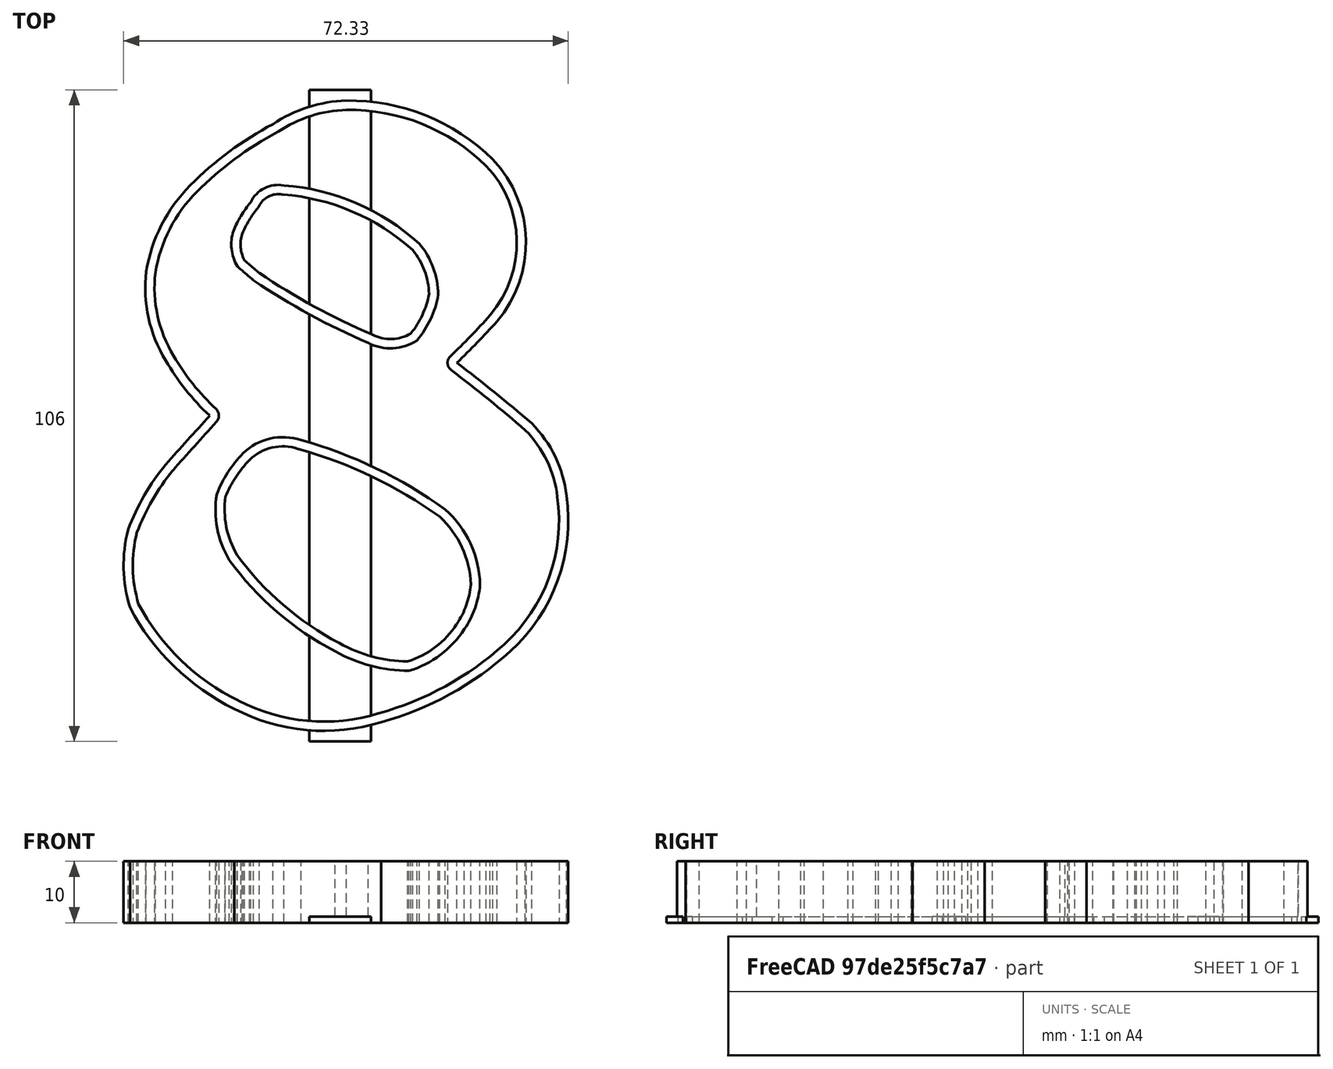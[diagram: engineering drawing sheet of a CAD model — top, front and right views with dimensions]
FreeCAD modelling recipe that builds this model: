
FCSTD DOCUMENT  (FreeCAD 0.20R27319 (Git))
Label: NumberCutter_8
License: All rights reserved
LicenseURL: http://en.wikipedia.org/wiki/All_rights_reserved
objects: Image::ImagePlane×1, Sketcher::SketchObject×1, PartDesign::Body×1, Part::Offset2D×1, Part::Extrusion×1, Part::Box×1, Part::MultiFuse×1
note: 6 computed .brp shape members not serialized (recipe doc carries the construction recipe); baked Part::Feature solids carry a one-line shape summary decoded from their .brp

FEATURE [Image::ImagePlane] ImagePlane
  XSize = 70
  YSize = 100
FEATURE [Sketcher::SketchObject] Sketch
  FullyConstrained = false
  MapMode = 5
  Support = -> [XY_Plane]
  sketch-geometry (35):
    g0: ArcOfCircle CenterX=0.458815 CenterY=17.8982 CenterZ=0 NormalX=0 NormalY=0 NormalZ=1 AngleXU=0 Radius=33.3475 StartAngle=0.793382 EndAngle=1.58456
    g1: ArcOfCircle CenterX=9.51677 CenterY=28.1376 CenterZ=0 NormalX=0 NormalY=0 NormalZ=1 AngleXU=0 Radius=19.7093 StartAngle=5.57634 EndAngle=7.0397
    g2: ArcOfCircle CenterX=-59.3448 CenterY=89.8945 CenterZ=0 NormalX=0 NormalY=0 NormalZ=1 AngleXU=0 Radius=112.202 StartAngle=5.47263 EndAngle=5.55638
    g3: ArcOfCircle CenterX=-125.944 CenterY=-181.615 CenterZ=0 NormalX=0 NormalY=0 NormalZ=1 AngleXU=0 Radius=238.513 StartAngle=0.857362 EndAngle=0.923044
    g4: ArcOfCircle CenterX=16.1082 CenterY=-15.2756 CenterZ=0 NormalX=0 NormalY=0 NormalZ=1 AngleXU=0 Radius=19.8297 StartAngle=0.113297 EndAngle=0.784184
    g5: ArcOfCircle CenterX=7.41771 CenterY=-17.0673 CenterZ=0 NormalX=0 NormalY=0 NormalZ=1 AngleXU=0 Radius=28.6781 StartAngle=5.44781 EndAngle=6.4243
    g6: ArcOfCircle CenterX=-8.01085 CenterY=-0.17681 CenterZ=0 NormalX=0 NormalY=0 NormalZ=1 AngleXU=0 Radius=51.5544 StartAngle=4.98143 EndAngle=5.44993
    g7: ArcOfCircle CenterX=-3.62359 CenterY=-19.767 CenterZ=0 NormalX=0 NormalY=0 NormalZ=1 AngleXU=0 Radius=31.5179 StartAngle=4.23045 EndAngle=5.01246
    g8: ArcOfCircle CenterX=-1.39127 CenterY=-13.4096 CenterZ=0 NormalX=0 NormalY=0 NormalZ=1 AngleXU=0 Radius=38.1982 StartAngle=3.62615 EndAngle=4.25581
    g9: ArcOfCircle CenterX=-13.0557 CenterY=-24.3418 CenterZ=0 NormalX=0 NormalY=0 NormalZ=1 AngleXU=0 Radius=23.1753 StartAngle=2.88854 EndAngle=3.44216
    g10: ArcOfCircle CenterX=0.145941 CenterY=-32.0737 CenterZ=0 NormalX=0 NormalY=0 NormalZ=1 AngleXU=0 Radius=38.1222 StartAngle=2.45633 EndAngle=2.77866
    g11: ArcOfCircle CenterX=-3185.35 CenterY=2837.49 CenterZ=0 NormalX=0 NormalY=0 NormalZ=1 AngleXU=0 Radius=4249.31 StartAngle=5.54949 EndAngle=5.552
    g12: ArcOfCircle CenterX=4.23687 CenterY=28.4722 CenterZ=0 NormalX=0 NormalY=0 NormalZ=1 AngleXU=0 Radius=38.8691 StartAngle=3.66706 EndAngle=3.9636
    g13: ArcOfCircle CenterX=-9.89684 CenterY=20.8136 CenterZ=0 NormalX=0 NormalY=0 NormalZ=1 AngleXU=0 Radius=22.8052 StartAngle=3.02569 EndAngle=3.68743
    g14: ArcOfCircle CenterX=-6.96797 CenterY=19.2324 CenterZ=0 NormalX=0 NormalY=0 NormalZ=1 AngleXU=0 Radius=25.9266 StartAngle=2.36127 EndAngle=2.97816
    g15: ArcOfCircle CenterX=14.8075 CenterY=-2.80678 CenterZ=0 NormalX=0 NormalY=0 NormalZ=1 AngleXU=0 Radius=56.9079 StartAngle=2.05998 EndAngle=2.35523
    g16: ArcOfCircle CenterX=0.649296 CenterY=28.6426 CenterZ=0 NormalX=0 NormalY=0 NormalZ=1 AngleXU=0 Radius=22.6093 StartAngle=1.59952 EndAngle=2.16102
    g17: ArcOfCircle CenterX=-0.898156 CenterY=22.6525 CenterZ=0 NormalX=0 NormalY=0 NormalZ=1 AngleXU=0 Radius=18.9841 StartAngle=2.45306 EndAngle=2.73929
    g18: ArcOfCircle CenterX=-11.4978 CenterY=27.8984 CenterZ=0 NormalX=0 NormalY=0 NormalZ=1 AngleXU=0 Radius=7.20861 StartAngle=2.83333 EndAngle=3.66939
    g19: ArcOfCircle CenterX=-11.049 CenterY=32.517 CenterZ=0 NormalX=0 NormalY=0 NormalZ=1 AngleXU=0 Radius=5.01561 StartAngle=1.39646 EndAngle=2.68795
    g20: ArcOfCircle CenterX=-12.9585 CenterY=0.610782 CenterZ=0 NormalX=0 NormalY=0 NormalZ=1 AngleXU=0 Radius=36.9505 StartAngle=0.834277 EndAngle=1.4955
    g21: ArcOfCircle CenterX=1.74944 CenterY=19.4754 CenterZ=0 NormalX=0 NormalY=0 NormalZ=1 AngleXU=0 Radius=13.2157 StartAngle=0.0123752 EndAngle=0.699498
    g22: ArcOfCircle CenterX=-0.714753 CenterY=22.4724 CenterZ=0 NormalX=0 NormalY=0 NormalZ=1 AngleXU=0 Radius=15.9328 StartAngle=5.58605 EndAngle=6.1044
    g23: ArcOfCircle CenterX=7.17885 CenterY=18.7713 CenterZ=0 NormalX=0 NormalY=0 NormalZ=1 AngleXU=0 Radius=7.8291 StartAngle=4.23267 EndAngle=5.29718
    g24: ArcOfCircle CenterX=47.9675 CenterY=115.345 CenterZ=0 NormalX=0 NormalY=0 NormalZ=1 AngleXU=0 Radius=112.64 StartAngle=4.11838 EndAngle=4.3072
    g25: ArcOfCircle CenterX=164.51 CenterY=234.501 CenterZ=0 NormalX=0 NormalY=0 NormalZ=1 AngleXU=0 Radius=278.222 StartAngle=3.99821 EndAngle=4.01074
    g26: ArcOfCircle CenterX=-2.0198 CenterY=-20.3667 CenterZ=0 NormalX=0 NormalY=0 NormalZ=1 AngleXU=0 Radius=20.5256 StartAngle=2.37591 EndAngle=2.76374
    g27: ArcOfCircle CenterX=-10.323 CenterY=-12.845 CenterZ=0 NormalX=0 NormalY=0 NormalZ=1 AngleXU=0 Radius=9.3329 StartAngle=1.2485 EndAngle=2.34035
    g28: ArcOfCircle CenterX=-27.2666 CenterY=-75.4573 CenterZ=0 NormalX=0 NormalY=0 NormalZ=1 AngleXU=0 Radius=74.1836 StartAngle=0.946292 EndAngle=1.29922
    g29: ArcOfCircle CenterX=4.70044 CenterY=-27.9477 CenterZ=0 NormalX=0 NormalY=0 NormalZ=1 AngleXU=0 Radius=17.0505 StartAngle=0.0263398 EndAngle=0.837857
    g30: ArcOfCircle CenterX=-5.28804 CenterY=-15.2888 CenterZ=0 NormalX=0 NormalY=0 NormalZ=1 AngleXU=0 Radius=16.0051 StartAngle=2.9851 EndAngle=3.68069
    g31: ArcOfCircle CenterX=21.4014 CenterY=5.95115 CenterZ=0 NormalX=0 NormalY=0 NormalZ=1 AngleXU=0 Radius=50.0182 StartAngle=3.7713 EndAngle=4.22901
    g32: ArcOfCircle CenterX=10.3781 CenterY=-16.3941 CenterZ=0 NormalX=0 NormalY=0 NormalZ=1 AngleXU=0 Radius=25.1175 StartAngle=4.20412 EndAngle=4.70526
    g33: ArcOfCircle CenterX=5.51619 CenterY=-25.9161 CenterZ=0 NormalX=0 NormalY=0 NormalZ=1 AngleXU=0 Radius=16.2827 StartAngle=5.0041 EndAngle=5.71123
    g34: ArcOfCircle CenterX=7.0438 CenterY=-26.4003 CenterZ=0 NormalX=0 NormalY=0 NormalZ=1 AngleXU=0 Radius=14.7422 StartAngle=5.68275 EndAngle=6.20861
  constraints (38):
    c: PointOnObject(g0,g-2)
    c: Coincident(g1,g0)
    c: Coincident(g2,g1)
    c: Coincident(g3,g2)
    c: Coincident(g4,g3)
    c: Coincident(g5,g4)
    c: Coincident(g6,g5)
    c: Coincident(g7,g6)
    c: Coincident(g8,g7)
    c: Coincident(g9,g8)
    c: Coincident(g10,g9)
    c: Coincident(g11,g10)
    c: PointOnObject(g11,g-1)
    c: Coincident(g12,g11)
    c: Coincident(g13,g12)
    c: Coincident(g14,g13)
    c: Coincident(g15,g14)
    c: Coincident(g16,g15)
    c: Coincident(g16,g0)
    c: Coincident(g18,g17)
    c: Coincident(g19,g17)
    c: Coincident(g20,g19)
    c: Coincident(g21,g20)
    c: Coincident(g22,g21)
    c: Coincident(g23,g22)
    c: Coincident(g24,g23)
    c: Coincident(g25,g18)
    c: Coincident(g25,g24)
    c: Coincident(g27,g26)
    c: Coincident(g28,g27)
    c: Coincident(g28,g4)
    c: Coincident(g29,g4)
    c: Coincident(g30,g26)
    c: Coincident(g31,g30)
    c: Coincident(g32,g31)
    c: Coincident(g33,g32)
    c: Coincident(g34,g33)
    c: Coincident(g34,g29)
FEATURE [PartDesign::Body] Body
  Group = -> [Sketch]
  Origin = -> Origin
FEATURE [Part::Offset2D] Offset2D
  Fill = true
  Intersection = false
  Join = 0
  Mode = 1
  SelfIntersection = false
  Source = -> Sketch
  Value = -1.5
FEATURE [Part::Extrusion] Extrude
  Base = -> Offset2D
  Dir = (0,0,1)
  DirMode = 2
  FaceMakerClass = Part::FaceMakerBullseye
  LengthFwd = 10
  LengthRev = 0
  Solid = true
  Symmetric = false
FEATURE [Part::Box] Box  label="Cube"
  AttacherType = Attacher::AttachEngine3D
  Height = 1
  Length = 10
  Placement = pos=(-6,-53,0) rot=(0,0,1;0rad)
  Width = 106
FEATURE [Part::MultiFuse] Fusion
  Shapes = -> [Extrude,Box]
